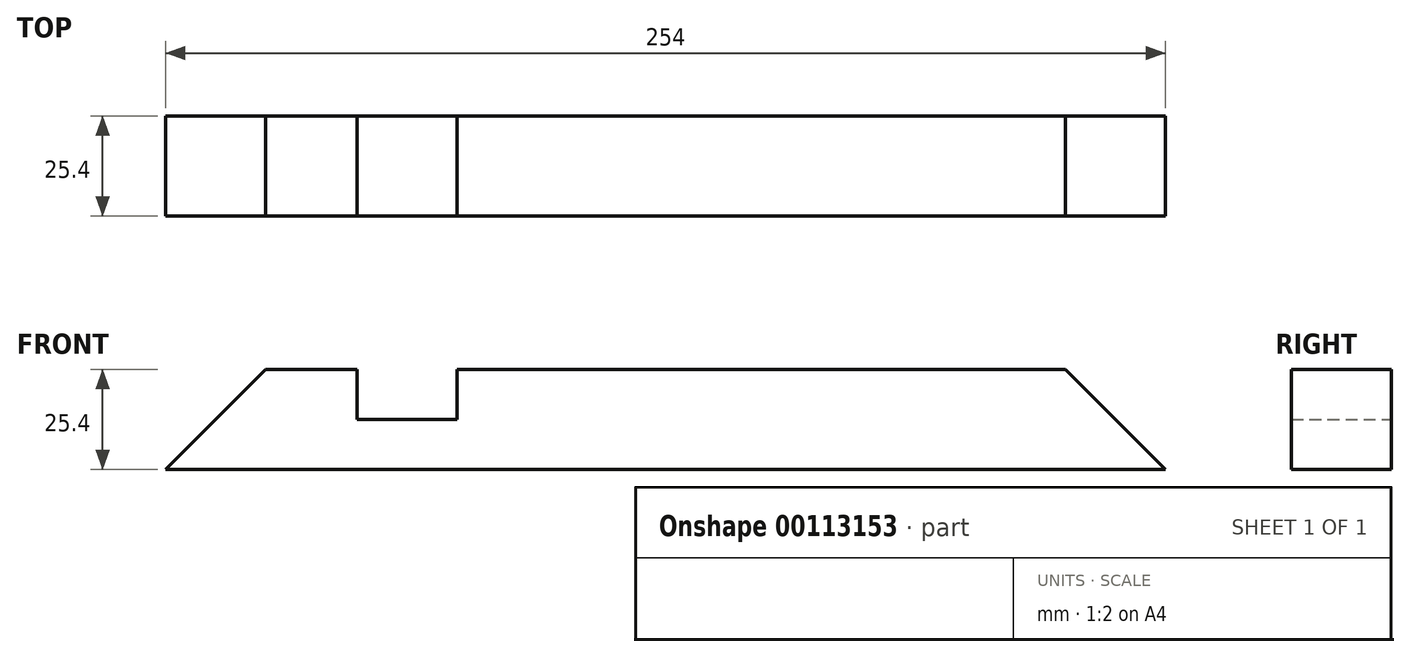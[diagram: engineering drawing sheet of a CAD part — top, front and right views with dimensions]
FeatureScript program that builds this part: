
annotation { "Feature Type Name" : "Feature", "Feature Type Description" : "" }
export const myFeature = defineFeature(function(context is Context, id is Id, definition is map)
    precondition{}
    {
        {
            var Q0;
            Q0=qCreatedBy(makeId("Front.planeOp"),FACE);
            var sketch = newSketch(context, id + "F0", { "sketchPlane" : qUnion([Q0])});
            skLineSegment(sketch, "E0.bottom", {"start": v(-74.77, -22.61) * mm, "end": v(179.23, -22.61) * mm});
            skLineSegment(sketch, "E0.top", {"start": v(-74.77, -48.01) * mm, "end": v(179.23, -48.01) * mm});
            skLineSegment(sketch, "E0.left", {"start": v(-74.77, -22.61) * mm, "end": v(-74.77, -48.01) * mm});
            skLineSegment(sketch, "E0.right", {"start": v(179.23, -22.61) * mm, "end": v(179.23, -48.01) * mm});
            skSolve(sketch);
        }
        {
            var Q0;
            Q0=makeQuery(id+"F0.imprint","IMPRINT",FACE,{"disambiguationData":[TD([[makeQuery(id+"F0.imprint","IMPRINT",EDGE,{"derivedFrom":sQuery(id+"F0.wireOp",EDGE,"E0.bottom")}),-1.0]])]});
            extrude(context, id + "F1", {"entities" : qUnion([Q0]), "oppositeDirection" : true, "depth" : 25.4 * mm});
        }
        {
            var Q0;
            Q0=makeQuery(id+"F1.opExtrude","SWEPT_EDGE",EDGE,{"disambiguationData":[OSD([sQuery(id+"F0.wireOp",EDGE,"E0.bottom"),sQuery(id+"F0.wireOp",EDGE,"E0.right")])]});
            chamfer(context, id + "F2", {"entities" : qUnion([Q0]), "chamferType" : ChamferType.OFFSET_ANGLE, "width" : 25.4 * mm, "oppositeDirection" : false, "angle" : 45 * degree, "tangentPropagation" : true});
        }
        {
            var Q0;
            Q0=makeQuery(id+"F1.opExtrude","SWEPT_EDGE",EDGE,{"disambiguationData":[OSD([sQuery(id+"F0.wireOp",EDGE,"E0.bottom"),sQuery(id+"F0.wireOp",EDGE,"E0.left")])]});
            chamfer(context, id + "F3", {"entities" : qUnion([Q0]), "chamferType" : ChamferType.OFFSET_ANGLE, "width" : 25.4 * mm, "oppositeDirection" : false, "angle" : 45 * degree, "tangentPropagation" : true});
        }
        {
            var Q0;
            Q0=makeQuery(id+"F1.opExtrude","SWEPT_FACE",FACE,{"disambiguationData":[OSD([sQuery(id+"F0.wireOp",EDGE,"E0.bottom")])]});
            var sketch = newSketch(context, id + "F4", { "sketchPlane" : qUnion([Q0])});
            skLineSegment(sketch, "E1.bottom", {"start": v(-26.14, 0) * mm, "end": v(-0.74, 0) * mm});
            skLineSegment(sketch, "E1.top", {"start": v(-26.14, 25.4) * mm, "end": v(-0.74, 25.4) * mm});
            skLineSegment(sketch, "E1.left", {"start": v(-26.14, 0) * mm, "end": v(-26.14, 25.4) * mm});
            skLineSegment(sketch, "E1.right", {"start": v(-0.74, 0) * mm, "end": v(-0.74, 25.4) * mm});
            skSolve(sketch);
        }
        {
            var Q0;
            Q0=makeQuery(id+"F4.imprint","IMPRINT",FACE,{"disambiguationData":[TD([[makeQuery(id+"F4.imprint","IMPRINT",EDGE,{"derivedFrom":sQuery(id+"F4.wireOp",EDGE,"E1.bottom")}),1.0]])]});
            extrude(context, id + "F5", {"entities" : qUnion([Q0]), "operationType" : NewBodyOperationType.REMOVE, "oppositeDirection" : true, "depth" : 12.7 * mm});
        }
    });
